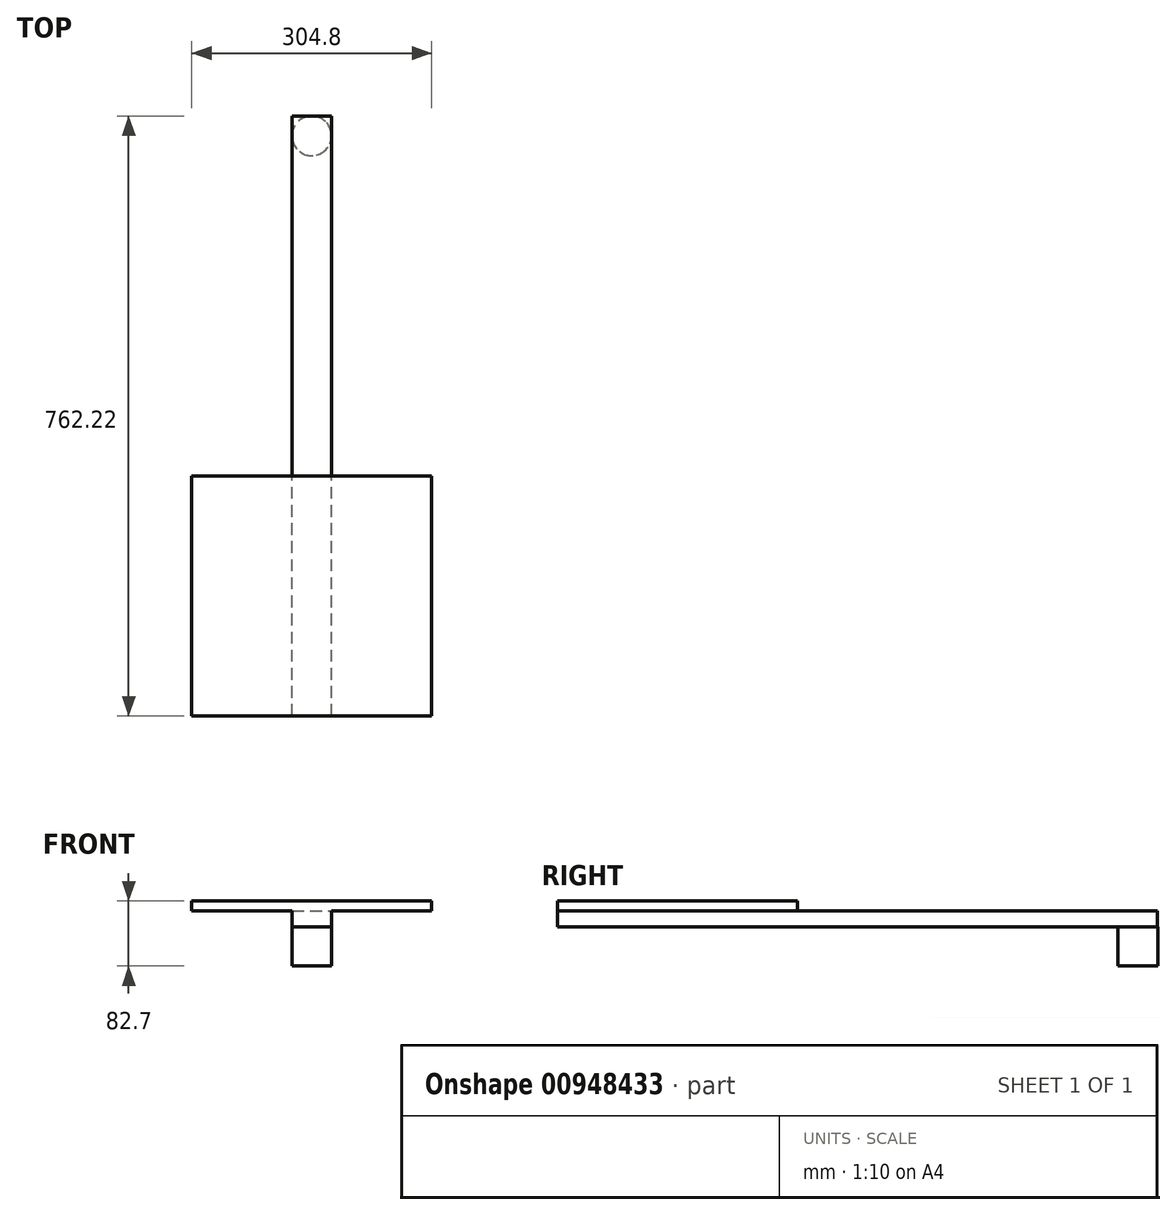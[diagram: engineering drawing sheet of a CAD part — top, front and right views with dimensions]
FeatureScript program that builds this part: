
annotation { "Feature Type Name" : "Feature", "Feature Type Description" : "" }
export const myFeature = defineFeature(function(context is Context, id is Id, definition is map)
    precondition{}
    {
        {
            var Q0;
            Q0=qCreatedBy(makeId("Front.planeOp"),FACE);
            var sketch = newSketch(context, id + "F0", { "sketchPlane" : qUnion([Q0])});
            skLineSegment(sketch, "E0.bottom", {"start": v(25, 10) * mm, "end": v(-25, 10) * mm});
            skLineSegment(sketch, "E0.top", {"start": v(25, -10) * mm, "end": v(-25, -10) * mm});
            skLineSegment(sketch, "E0.left", {"start": v(25, 10) * mm, "end": v(25, -10) * mm});
            skLineSegment(sketch, "E0.right", {"start": v(-25, 10) * mm, "end": v(-25, -10) * mm});
            skPoint(sketch, "E0.middle", {"position": v(0, 0) * mm});
            skSolve(sketch);
        }
        {
            var Q0;
            Q0 = qSketchRegion(id + "F0", true);
            extrude(context, id + "F1", {"entities" : qUnion([Q0]), "endBound" : BoundingType.SYMMETRIC, "depth" : 762 * mm, "offsetDistance" : 25 * mm});
        }
        {
            var Q0;
            Q0=makeQuery(id+"F1.opExtrude","SWEPT_FACE",FACE,{"disambiguationData":[OSD([sQuery(id+"F0.wireOp",EDGE,"E0.top")])]});
            var sketch = newSketch(context, id + "F2", { "sketchPlane" : qUnion([Q0])});
            skLineSegment(sketch, "E1", {"start": v(0, -381) * mm, "end": v(0, -356) * mm});
            skCircle(sketch, "E2", {"center": v(0, -356) * mm, "radius": 25.22 * mm});
            skSolve(sketch);
        }
        {
            var Q0;
            Q0 = qSketchRegion(id + "F2", true);
            extrude(context, id + "F3", {"entities" : qUnion([Q0]), "operationType" : NewBodyOperationType.ADD, "depth" : 50 * mm, "offsetDistance" : 25 * mm});
        }
        {
            var Q0;
            Q0=makeQuery(id+"F1.opExtrude","SWEPT_FACE",FACE,{"disambiguationData":[OSD([sQuery(id+"F0.wireOp",EDGE,"E0.bottom")])]});
            var sketch = newSketch(context, id + "F4", { "sketchPlane" : qUnion([Q0])});
            skLineSegment(sketch, "E3", {"start": v(0, -381) * mm, "end": v(0, -228.6) * mm});
            skLineSegment(sketch, "E4.bottom", {"start": v(-152.4, -381) * mm, "end": v(152.4, -381) * mm});
            skLineSegment(sketch, "E4.top", {"start": v(-152.4, -76.2) * mm, "end": v(152.4, -76.2) * mm});
            skLineSegment(sketch, "E4.left", {"start": v(-152.4, -381) * mm, "end": v(-152.4, -76.2) * mm});
            skLineSegment(sketch, "E4.right", {"start": v(152.4, -381) * mm, "end": v(152.4, -76.2) * mm});
            skPoint(sketch, "E4.middle", {"position": v(0, -228.6) * mm});
            skSolve(sketch);
        }
        {
            var Q0;
            Q0 = qSketchRegion(id + "F4", true);
            extrude(context, id + "F5", {"entities" : qUnion([Q0]), "operationType" : NewBodyOperationType.ADD, "depth" : 12.7 * mm, "offsetDistance" : 25 * mm});
        }
    });
